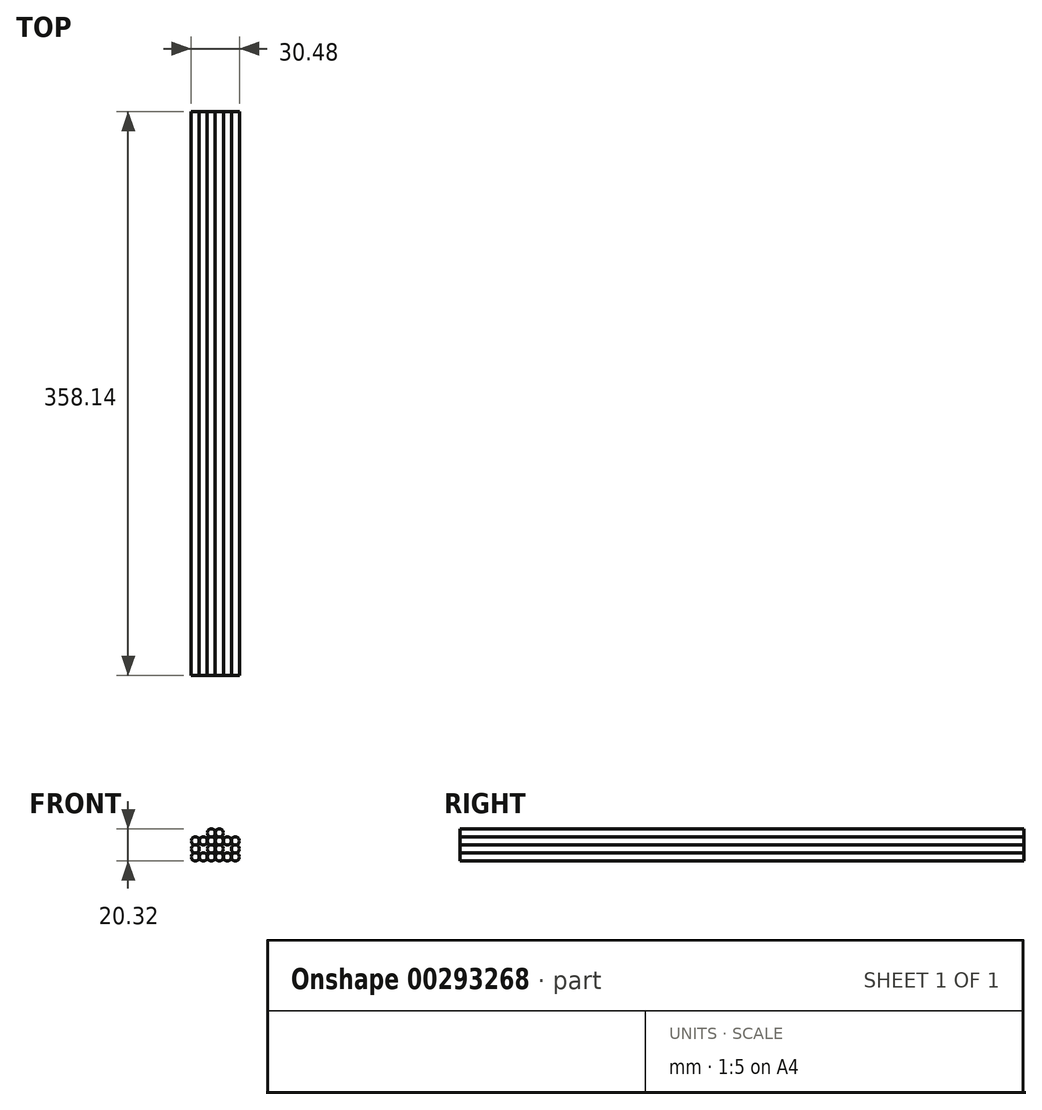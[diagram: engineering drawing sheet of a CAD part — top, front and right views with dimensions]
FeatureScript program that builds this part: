
annotation { "Feature Type Name" : "Feature", "Feature Type Description" : "" }
export const myFeature = defineFeature(function(context is Context, id is Id, definition is map)
    precondition{}
    {
        {
            var Q0;
            Q0=qCreatedBy(makeId("Front.planeOp"),FACE);
            var sketch = newSketch(context, id + "F0", { "sketchPlane" : qUnion([Q0])});
            skCircle(sketch, "E0", {"center": v(0, 0) * mm, "radius": 2.54 * mm});
            skCircle(sketch, "E1", {"center": v(10.16, 0) * mm, "radius": 2.54 * mm});
            skCircle(sketch, "E2", {"center": v(5.08, 0) * mm, "radius": 2.54 * mm});
            skCircle(sketch, "E3", {"center": v(15.24, 0) * mm, "radius": 2.54 * mm});
            skCircle(sketch, "E4", {"center": v(20.32, 0) * mm, "radius": 2.54 * mm});
            skCircle(sketch, "E5", {"center": v(10.16, -5.08) * mm, "radius": 2.54 * mm});
            skCircle(sketch, "E6", {"center": v(10.16, -10.16) * mm, "radius": 2.54 * mm});
            skCircle(sketch, "E7", {"center": v(0, -10.16) * mm, "radius": 2.54 * mm});
            skCircle(sketch, "E8", {"center": v(0, -5.08) * mm, "radius": 2.54 * mm});
            skCircle(sketch, "E9", {"center": v(5.08, -10.16) * mm, "radius": 2.54 * mm});
            skCircle(sketch, "E10", {"center": v(15.24, -10.16) * mm, "radius": 2.54 * mm});
            skCircle(sketch, "E11", {"center": v(20.32, -10.16) * mm, "radius": 2.54 * mm});
            skCircle(sketch, "E12", {"center": v(25.4, -10.16) * mm, "radius": 2.54 * mm});
            skCircle(sketch, "E13", {"center": v(25.4, 0) * mm, "radius": 2.54 * mm});
            skCircle(sketch, "E14", {"center": v(15.24, -5.08) * mm, "radius": 2.54 * mm});
            skCircle(sketch, "E15", {"center": v(10.16, 5.08) * mm, "radius": 2.54 * mm});
            skCircle(sketch, "E16", {"center": v(25.4, -5.08) * mm, "radius": 2.54 * mm});
            skCircle(sketch, "E17", {"center": v(15.24, 5.08) * mm, "radius": 2.54 * mm});
            skSolve(sketch);
        }
        {
            var Q0;
            {var subQ0=sQuery(id+"F0.wireOp",EDGE,"E2");var subQ1=makeQuery(id+"F0.imprint","INTERSECT",VERTEX,{"derivedFrom":[sQuery(id+"F0.wireOp",EDGE,"E0"),subQ0]});Q0=makeQuery(id+"F0.imprint","IMPRINT",FACE,{"disambiguationData":[TD([[makeQuery(id+"F0.imprint","IMPRINT",EDGE,{"disambiguationData":[TD([[subQ1,1.0]])],"derivedFrom":subQ0}),1.0]])]});}
            var Q1;
            {var subQ0=sQuery(id+"F0.wireOp",EDGE,"E0");var subQ1=makeQuery(id+"F0.imprint","INTERSECT",VERTEX,{"derivedFrom":[subQ0,sQuery(id+"F0.wireOp",EDGE,"E2")]});Q1=makeQuery(id+"F0.imprint","IMPRINT",FACE,{"disambiguationData":[TD([[makeQuery(id+"F0.imprint","IMPRINT",EDGE,{"disambiguationData":[TD([[subQ1,-1.0]])],"derivedFrom":subQ0}),1.0]])]});}
            var Q2;
            {var subQ0=sQuery(id+"F0.wireOp",EDGE,"E8");var subQ1=makeQuery(id+"F0.imprint","INTERSECT",VERTEX,{"derivedFrom":[sQuery(id+"F0.wireOp",EDGE,"E0"),subQ0]});Q2=makeQuery(id+"F0.imprint","IMPRINT",FACE,{"disambiguationData":[TD([[makeQuery(id+"F0.imprint","IMPRINT",EDGE,{"disambiguationData":[TD([[subQ1,-1.0]])],"derivedFrom":subQ0}),1.0]])]});}
            var Q3;
            {var subQ0=sQuery(id+"F0.wireOp",EDGE,"E7");var subQ1=makeQuery(id+"F0.imprint","INTERSECT",VERTEX,{"derivedFrom":[subQ0,sQuery(id+"F0.wireOp",EDGE,"E8")]});Q3=makeQuery(id+"F0.imprint","IMPRINT",FACE,{"disambiguationData":[TD([[makeQuery(id+"F0.imprint","IMPRINT",EDGE,{"disambiguationData":[TD([[subQ1,1.0]])],"derivedFrom":subQ0}),1.0]])]});}
            var Q4;
            {var subQ0=sQuery(id+"F0.wireOp",EDGE,"E9");var subQ1=makeQuery(id+"F0.imprint","INTERSECT",VERTEX,{"derivedFrom":[sQuery(id+"F0.wireOp",EDGE,"E6"),subQ0]});Q4=makeQuery(id+"F0.imprint","IMPRINT",FACE,{"disambiguationData":[TD([[makeQuery(id+"F0.imprint","IMPRINT",EDGE,{"disambiguationData":[TD([[subQ1,-1.0]])],"derivedFrom":subQ0}),1.0]])]});}
            var Q5;
            {var subQ0=sQuery(id+"F0.wireOp",EDGE,"E6");var subQ1=makeQuery(id+"F0.imprint","INTERSECT",VERTEX,{"derivedFrom":[subQ0,sQuery(id+"F0.wireOp",EDGE,"E10")]});Q5=makeQuery(id+"F0.imprint","IMPRINT",FACE,{"disambiguationData":[TD([[makeQuery(id+"F0.imprint","IMPRINT",EDGE,{"disambiguationData":[TD([[subQ1,-1.0]])],"derivedFrom":subQ0}),1.0]])]});}
            var Q6;
            {var subQ0=sQuery(id+"F0.wireOp",EDGE,"E5");var subQ1=makeQuery(id+"F0.imprint","INTERSECT",VERTEX,{"derivedFrom":[sQuery(id+"F0.wireOp",EDGE,"E1"),subQ0]});Q6=makeQuery(id+"F0.imprint","IMPRINT",FACE,{"disambiguationData":[TD([[makeQuery(id+"F0.imprint","IMPRINT",EDGE,{"disambiguationData":[TD([[subQ1,1.0]])],"derivedFrom":subQ0}),1.0]])]});}
            var Q7;
            {var subQ0=sQuery(id+"F0.wireOp",EDGE,"E1");var subQ1=makeQuery(id+"F0.imprint","INTERSECT",VERTEX,{"derivedFrom":[subQ0,sQuery(id+"F0.wireOp",EDGE,"E2")]});Q7=makeQuery(id+"F0.imprint","IMPRINT",FACE,{"disambiguationData":[TD([[makeQuery(id+"F0.imprint","IMPRINT",EDGE,{"disambiguationData":[TD([[subQ1,1.0]])],"derivedFrom":subQ0}),1.0]])]});}
            var Q8;
            {var subQ0=sQuery(id+"F0.wireOp",EDGE,"E15");var subQ1=makeQuery(id+"F0.imprint","INTERSECT",VERTEX,{"derivedFrom":[sQuery(id+"F0.wireOp",EDGE,"E1"),subQ0]});Q8=makeQuery(id+"F0.imprint","IMPRINT",FACE,{"disambiguationData":[TD([[makeQuery(id+"F0.imprint","IMPRINT",EDGE,{"disambiguationData":[TD([[subQ1,-1.0]])],"derivedFrom":subQ0}),1.0]])]});}
            var Q9;
            {var subQ0=sQuery(id+"F0.wireOp",EDGE,"E17");var subQ1=makeQuery(id+"F0.imprint","INTERSECT",VERTEX,{"derivedFrom":[sQuery(id+"F0.wireOp",EDGE,"E3"),subQ0]});Q9=makeQuery(id+"F0.imprint","IMPRINT",FACE,{"disambiguationData":[TD([[makeQuery(id+"F0.imprint","IMPRINT",EDGE,{"disambiguationData":[TD([[subQ1,1.0]])],"derivedFrom":subQ0}),1.0]])]});}
            var Q10;
            {var subQ0=sQuery(id+"F0.wireOp",EDGE,"E3");var subQ1=makeQuery(id+"F0.imprint","INTERSECT",VERTEX,{"derivedFrom":[subQ0,sQuery(id+"F0.wireOp",EDGE,"E17")]});Q10=makeQuery(id+"F0.imprint","IMPRINT",FACE,{"disambiguationData":[TD([[makeQuery(id+"F0.imprint","IMPRINT",EDGE,{"disambiguationData":[TD([[subQ1,-1.0]])],"derivedFrom":subQ0}),1.0]])]});}
            var Q11;
            {var subQ0=sQuery(id+"F0.wireOp",EDGE,"E14");var subQ1=makeQuery(id+"F0.imprint","INTERSECT",VERTEX,{"derivedFrom":[sQuery(id+"F0.wireOp",EDGE,"E3"),subQ0]});Q11=makeQuery(id+"F0.imprint","IMPRINT",FACE,{"disambiguationData":[TD([[makeQuery(id+"F0.imprint","IMPRINT",EDGE,{"disambiguationData":[TD([[subQ1,-1.0]])],"derivedFrom":subQ0}),1.0]])]});}
            var Q12;
            {var subQ0=sQuery(id+"F0.wireOp",EDGE,"E10");var subQ1=makeQuery(id+"F0.imprint","INTERSECT",VERTEX,{"derivedFrom":[sQuery(id+"F0.wireOp",EDGE,"E6"),subQ0]});Q12=makeQuery(id+"F0.imprint","IMPRINT",FACE,{"disambiguationData":[TD([[makeQuery(id+"F0.imprint","IMPRINT",EDGE,{"disambiguationData":[TD([[subQ1,1.0]])],"derivedFrom":subQ0}),1.0]])]});}
            var Q13;
            {var subQ0=sQuery(id+"F0.wireOp",EDGE,"E11");var subQ1=makeQuery(id+"F0.imprint","INTERSECT",VERTEX,{"derivedFrom":[sQuery(id+"F0.wireOp",EDGE,"E10"),subQ0]});Q13=makeQuery(id+"F0.imprint","IMPRINT",FACE,{"disambiguationData":[TD([[makeQuery(id+"F0.imprint","IMPRINT",EDGE,{"disambiguationData":[TD([[subQ1,1.0]])],"derivedFrom":subQ0}),1.0]])]});}
            var Q14;
            {var subQ0=sQuery(id+"F0.wireOp",EDGE,"E12");var subQ1=makeQuery(id+"F0.imprint","INTERSECT",VERTEX,{"derivedFrom":[sQuery(id+"F0.wireOp",EDGE,"E11"),subQ0]});Q14=makeQuery(id+"F0.imprint","IMPRINT",FACE,{"disambiguationData":[TD([[makeQuery(id+"F0.imprint","IMPRINT",EDGE,{"disambiguationData":[TD([[subQ1,1.0]])],"derivedFrom":subQ0}),1.0]])]});}
            var Q15;
            {var subQ0=sQuery(id+"F0.wireOp",EDGE,"E16");var subQ1=makeQuery(id+"F0.imprint","INTERSECT",VERTEX,{"derivedFrom":[sQuery(id+"F0.wireOp",EDGE,"E12"),subQ0]});Q15=makeQuery(id+"F0.imprint","IMPRINT",FACE,{"disambiguationData":[TD([[makeQuery(id+"F0.imprint","IMPRINT",EDGE,{"disambiguationData":[TD([[subQ1,1.0]])],"derivedFrom":subQ0}),1.0]])]});}
            var Q16;
            {var subQ0=sQuery(id+"F0.wireOp",EDGE,"E13");var subQ1=makeQuery(id+"F0.imprint","INTERSECT",VERTEX,{"derivedFrom":[sQuery(id+"F0.wireOp",EDGE,"E4"),subQ0]});Q16=makeQuery(id+"F0.imprint","IMPRINT",FACE,{"disambiguationData":[TD([[makeQuery(id+"F0.imprint","IMPRINT",EDGE,{"disambiguationData":[TD([[subQ1,-1.0]])],"derivedFrom":subQ0}),1.0]])]});}
            var Q17;
            {var subQ0=sQuery(id+"F0.wireOp",EDGE,"E4");var subQ1=makeQuery(id+"F0.imprint","INTERSECT",VERTEX,{"derivedFrom":[sQuery(id+"F0.wireOp",EDGE,"E3"),subQ0]});Q17=makeQuery(id+"F0.imprint","IMPRINT",FACE,{"disambiguationData":[TD([[makeQuery(id+"F0.imprint","IMPRINT",EDGE,{"disambiguationData":[TD([[subQ1,-1.0]])],"derivedFrom":subQ0}),1.0]])]});}
            extrude(context, id + "F1", {"entities" : qUnion([Q0, Q1, Q2, Q3, Q4, Q5, Q6, Q7, Q8, Q9, Q10, Q11, Q12, Q13, Q14, Q15, Q16, Q17]), "depth" : 358.14 * mm});
        }
    });
